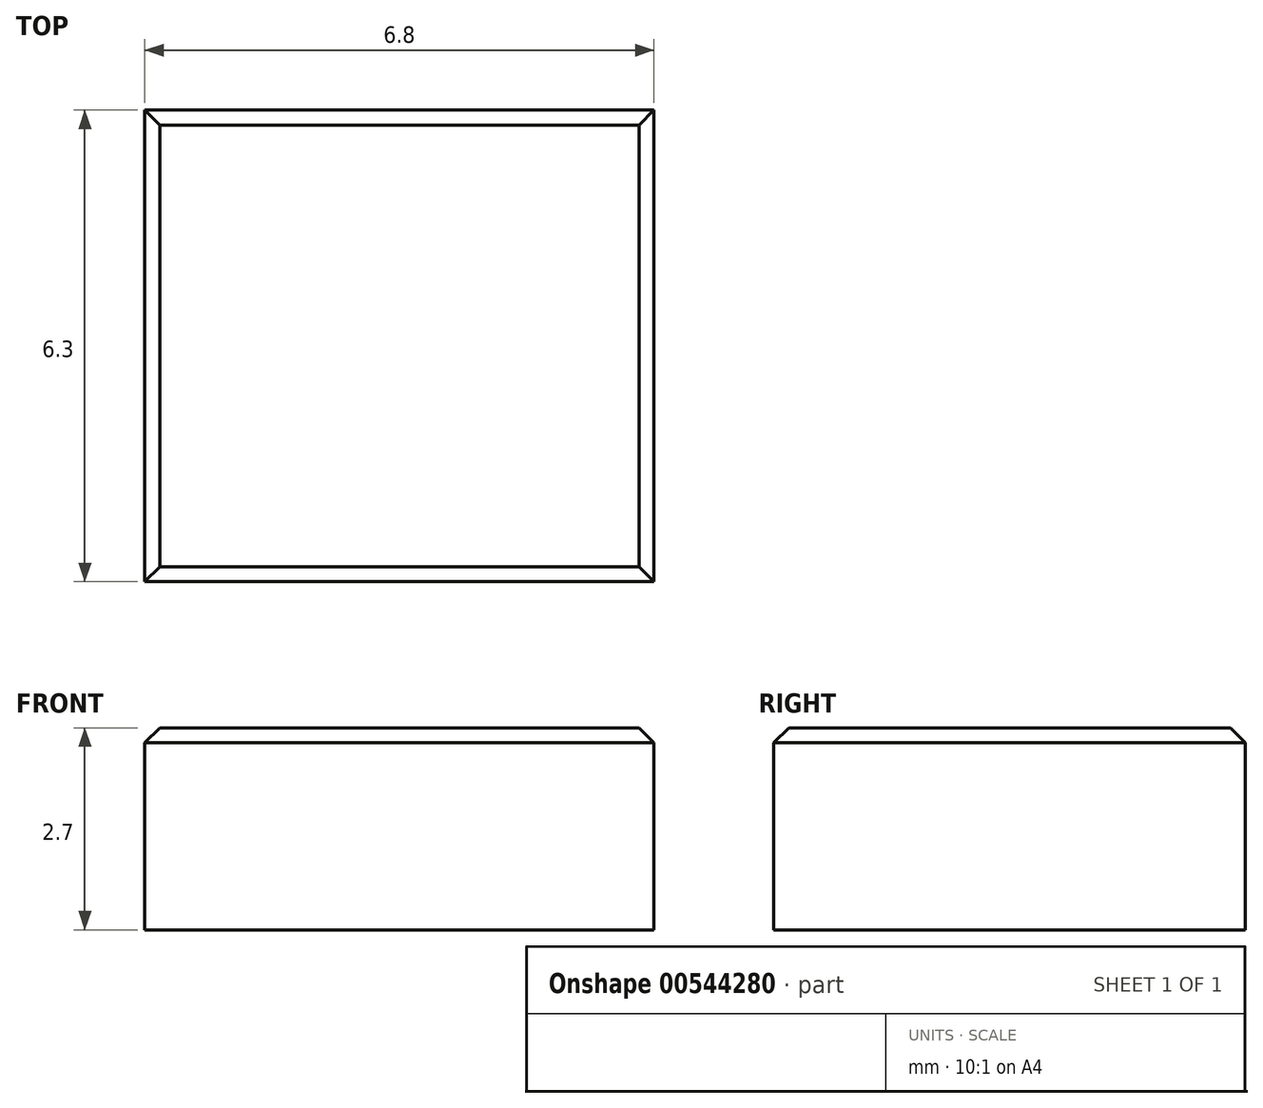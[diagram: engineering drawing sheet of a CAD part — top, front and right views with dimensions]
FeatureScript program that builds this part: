
annotation { "Feature Type Name" : "Feature", "Feature Type Description" : "" }
export const myFeature = defineFeature(function(context is Context, id is Id, definition is map)
    precondition{}
    {
        {
            var Q0;
            Q0=qCreatedBy(makeId("Top.planeOp"),FACE);
            var sketch = newSketch(context, id + "F0", { "sketchPlane" : qUnion([Q0])});
            skLineSegment(sketch, "E0.bottom", {"start": v(0, 0) * mm, "end": v(6.8, 0) * mm});
            skLineSegment(sketch, "E0.top", {"start": v(0, 6.3) * mm, "end": v(6.8, 6.3) * mm});
            skLineSegment(sketch, "E0.left", {"start": v(0, 0) * mm, "end": v(0, 6.3) * mm});
            skLineSegment(sketch, "E0.right", {"start": v(6.8, 0) * mm, "end": v(6.8, 6.3) * mm});
            skSolve(sketch);
        }
        {
            var Q0;
            Q0=qSketchRegion(id+"F0",true);
            extrude(context, id + "F1", {"entities" : qUnion([Q0]), "depth" : 2.7 * mm});
        }
        {
            var Q0;
            Q0=makeQuery(id+"F1.opExtrude","CAP_EDGE",EDGE,{"disambiguationData":[OSD([sQuery(id+"F0.wireOp",EDGE,"E0.bottom")])],"isStart":false});
            var Q1;
            Q1=makeQuery(id+"F1.opExtrude","CAP_EDGE",EDGE,{"disambiguationData":[OSD([sQuery(id+"F0.wireOp",EDGE,"E0.left")])],"isStart":false});
            var Q2;
            Q2=makeQuery(id+"F1.opExtrude","CAP_EDGE",EDGE,{"disambiguationData":[OSD([sQuery(id+"F0.wireOp",EDGE,"E0.top")])],"isStart":false});
            var Q3;
            Q3=makeQuery(id+"F1.opExtrude","CAP_EDGE",EDGE,{"disambiguationData":[OSD([sQuery(id+"F0.wireOp",EDGE,"E0.right")])],"isStart":false});
            chamfer(context, id + "F2", {"entities" : qUnion([Q0, Q1, Q2, Q3]), "width" : 0.2 * mm, "tangentPropagation" : true});
        }
    });
